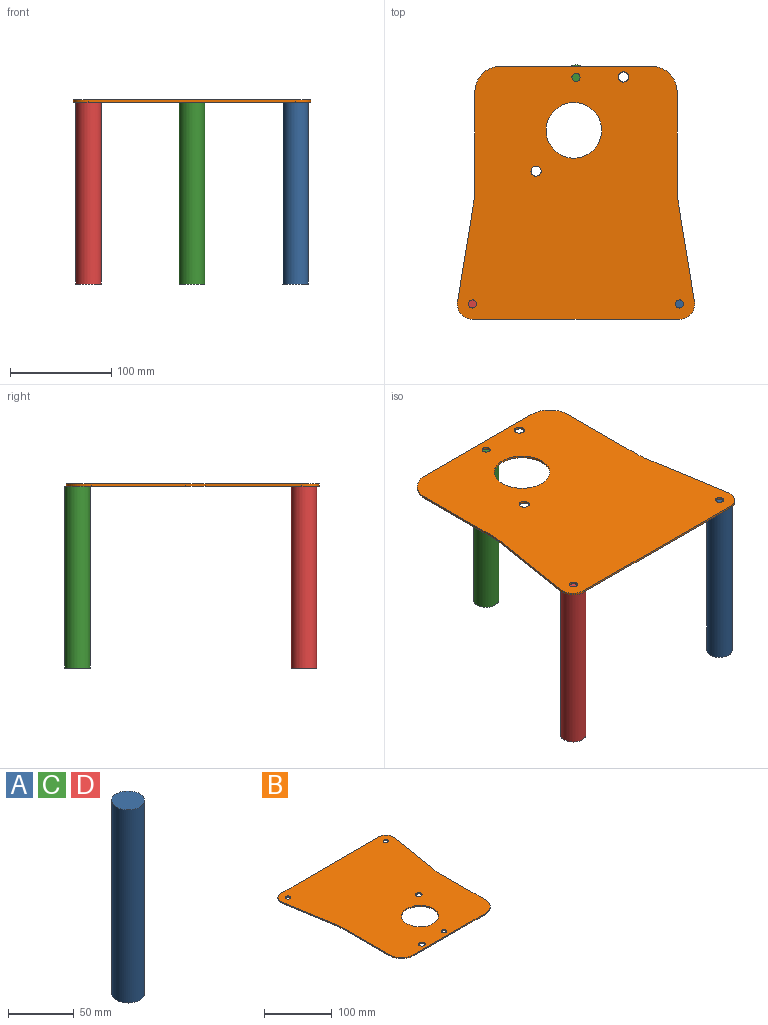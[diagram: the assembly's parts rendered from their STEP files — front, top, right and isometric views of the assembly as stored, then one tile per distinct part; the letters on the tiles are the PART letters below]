
ASSEMBLY  parts=4 mates=3
PART A: 3 faces, bbox 25x25x180 mm
  f0: cylinder r=12.5mm len=180mm, axis (0,0,-1), area 14137.2mm2, adj f1,f2
  f1: plane 25x25mm, normal (0,0,1), area 490.9mm2, adj f0
  f2: plane 25x25mm, normal (0,0,-1), area 490.9mm2, adj f0
PART B: 20 faces, bbox 234.7x250x2 mm
  f0: plane 92.78x2mm, normal (-1,0,0), area 185.6mm2, adj f1,f16,f18,f19
  f1: cylinder r=25mm len=25mm, axis (0,0,-1), area 78.5mm2, adj f0,f2,f18,f19
  f2: plane 150x2mm, normal (0,-1,0), area 300mm2, adj f1,f3,f18,f19
  f3: cylinder r=25mm len=25mm, axis (0,0,-1), area 78.5mm2, adj f2,f4,f18,f19
  f4: plane 92.78x2mm, normal (1,0,0), area 185.6mm2, adj f3,f5,f18,f19
  f5: cylinder r=120mm len=19.34mm, axis (0,0,-1), area 38.8mm2, adj f4,f6,f18,f19
  f6: plane 95.46x15.59mm, normal (0.99,-0.16,0), area 193.4mm2, adj f5,f7,f18,f19
  f7: cylinder r=15mm len=17.42mm, axis (0,0,-1), area 52mm2, adj f6,f8,f18,f19
  f8: plane 204.7x2mm, normal (0,1,0), area 409.4mm2, adj f7,f9,f18,f19
  f9: cylinder r=15mm len=17.42mm, axis (0,0,-1), area 52mm2, adj f8,f10,f18,f19
  f10: plane 95.46x15.59mm, normal (-0.99,-0.16,0), area 193.4mm2, adj f9,f16,f18,f19
  f11: cylinder r=4mm len=8mm, axis (0,0,-1), area 50.3mm2, adj f18,f19
  f12: cylinder r=4mm len=8mm, axis (0,0,-1), area 50.3mm2, adj f18,f19
  f13: cylinder r=5mm len=10mm, axis (0,0,-1), area 62.8mm2, adj f18,f19
  f14: cylinder r=5mm len=10mm, axis (0,0,-1), area 62.8mm2, adj f18,f19
  f15: cylinder r=27.5mm len=55mm, axis (0,0,-1), area 345.6mm2, adj f18,f19
  f16: cylinder r=120mm len=19.34mm, axis (0,0,-1), area 38.8mm2, adj f0,f10,f18,f19
  f17: cylinder r=4mm len=8mm, axis (0,0,-1), area 50.3mm2, adj f18,f19
  f18: plane 250x234.7mm, normal (0,0,1), area 49363.2mm2, adj f0,f1,f2,f3,f4,f5,f6,f7
  f19: plane 250x234.7mm, normal (0,0,-1), area 49363.2mm2, adj f0,f1,f2,f3,f4,f5,f6,f7
PART C: same geometry as A
PART D: same geometry as A
PLACE A t=(46.96,-144.95,-190.98)mm
PLACE B rot(axis=(0,0,1),180deg) t=(44.6,90.05,-10.98)mm
PLACE C t=(-55.4,79.05,-190.98)mm
PLACE D t=(-157.75,-144.95,-190.98)mm
MATE fastened B.f12 <-> C.f0  axis (0,0,-1) through (-55.4,79.05,-10.98)mm
MATE fastened B.f7 <-> D.f0  axis (0,0,-1) through (-157.75,-144.95,-10.98)mm
MATE fastened B.f9 <-> A.f0  axis (0,0,-1) through (46.96,-144.95,-10.98)mm
